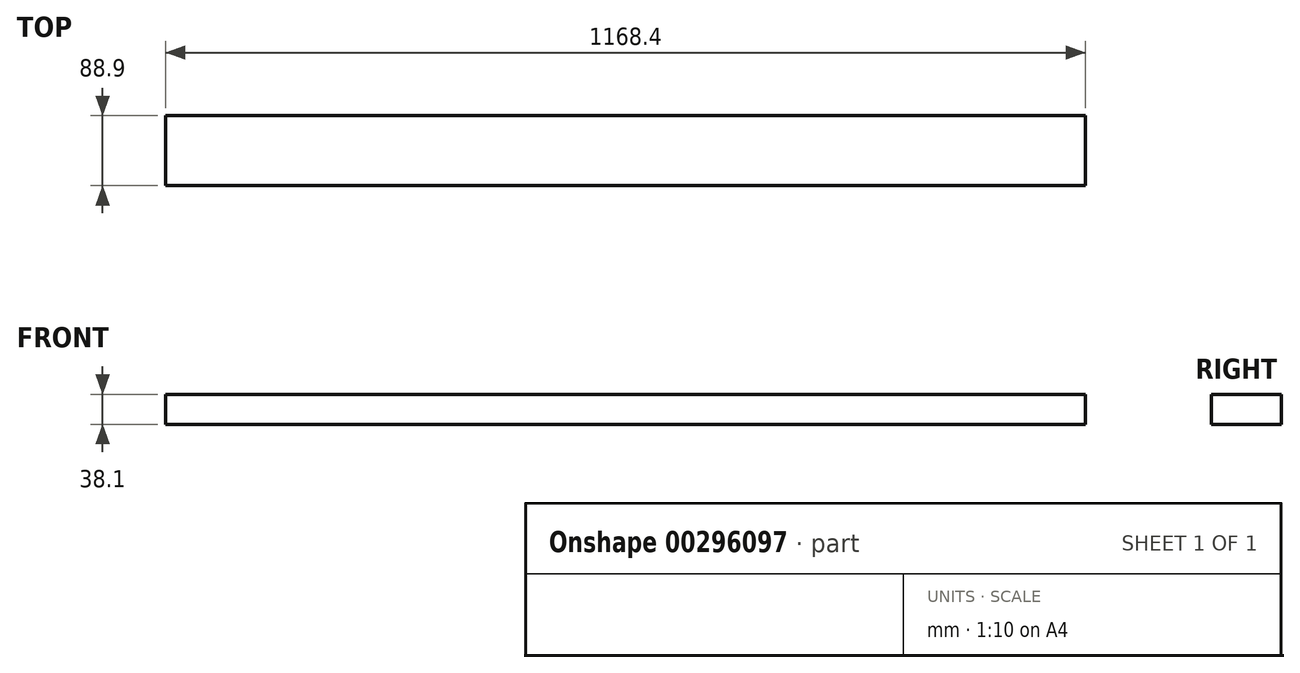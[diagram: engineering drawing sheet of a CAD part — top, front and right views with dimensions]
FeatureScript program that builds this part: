
annotation { "Feature Type Name" : "Feature", "Feature Type Description" : "" }
export const myFeature = defineFeature(function(context is Context, id is Id, definition is map)
    precondition{}
    {
        {
            var Q0;
            Q0=qCreatedBy(makeId("Front.planeOp"),FACE);
            var sketch = newSketch(context, id + "F0", { "sketchPlane" : qUnion([Q0])});
            skLineSegment(sketch, "E0.bottom", {"start": v(584.2, 19.05) * mm, "end": v(-584.2, 19.05) * mm});
            skLineSegment(sketch, "E0.top", {"start": v(584.2, -19.05) * mm, "end": v(-584.2, -19.05) * mm});
            skLineSegment(sketch, "E0.left", {"start": v(584.2, 19.05) * mm, "end": v(584.2, -19.05) * mm});
            skLineSegment(sketch, "E0.right", {"start": v(-584.2, 19.05) * mm, "end": v(-584.2, -19.05) * mm});
            skPoint(sketch, "E0.middle", {"position": v(0, 0) * mm});
            skSolve(sketch);
        }
        {
            var Q0;
            Q0=makeQuery(id+"F0.imprint","IMPRINT",FACE,{"disambiguationData":[TD([[makeQuery(id+"F0.imprint","IMPRINT",EDGE,{"derivedFrom":sQuery(id+"F0.wireOp",EDGE,"E0.bottom")}),1.0]])]});
            extrude(context, id + "F1", {"entities" : qUnion([Q0]), "depth" : 88.9 * mm});
        }
    });
